# Revit family: Electronics_Desono_Biamp_Two-Way-Pendant-Mount-Loudspeaker_P60DT
name_source: partatom
category: Communication Devices
units: mm (PartAtom-declared; Revit-internal decimal feet)

## family parameters
Cut with Voids When Loaded = No
Host = Face
Maintain Annotation Orientation = No
OmniClass Number = 23.85.10.11.14.14.14
OmniClass Title = Loudspeakers
Part Type = Normal
Room Calculation Point = No
Round Connector Dimension = Use Diameter
Shared = No

## types (2) — shared parameters
Compliance = ETL listed to comply with UL Std 1480A,Certifed to CSA C22.2#62368-1Suspension system and Gripple cable fasteners listed per UL1598 and UL2239, TUV and CSA Class 3426-01 and Class 3426-81.
Connector Description = Euroblock; Low Impedance 8 ohms, 70/100V operation
Continuous Power Handling Nominal Impedance = 31V; 60W @ 16Ω (240W peak)
Controls = Power tap / low impedance selector switch
Default Elevation = 4' - 0"
Description = Desono™ P60DT Two-Way 6.5-Inch Pendant Mount Loudspeaker
Diameter = 0' - 11"
Height = 0' - 10 1/2"
Input Connection = 4-way Euroblock connector with permanent pass-through
Manufacturer = Biamp
Mounting Provisions = Two 5m (16.4 ft) wire suspension cables (one as primary support, one as a safety cable), of high tensile galvanized steel wire rope with integrated spring clips for attaching the cable to the bracket and Gripple cable fasteners.
Nominal Beamwidth  (H x V) = 120°, conical
Nominal Maximum SPL @ 1m = Peak-113dB; Continuous-107dB)
Nominal Sensitivity @ 1m = 1W-89dB; 2.83V 86dB)
Operating Environment = Indoor
Operating Mode = Passive
Operating Range (-10dB) = 75 Hz to 22 kHz
Product Documentation Link = https://downloads.biamp.com
Product Page URL = https://www.biamp.com
Product data url = https://www.bimobject.com
Protection = Self-resetting loudspeaker protection
Recommended Accessories = 75 Hz, 12dB/Oct High Pass
Recommended Amplifers = 60W - 120W @ 16Ω (31V - 44V)
Transducers = LF 1 x 6.5 (165 mm) coated paper cone HF 1 x 1 (25 mm) soft dome
Transformer = 70V: 60W, 30W, 15W, 7.5W, 3.75W;100V: 60W, 30W, 15W, 7.5W
URL = https://www.biamp.com
Weight = 8.60 lb

## per-type parameters (varying)
| type | Bracket Material | Grill Material | Housing Material |
| P60DT W | Biamp - Metal - White | Biamp - Plastic - White(Grid) | Biamp - Plastic - White |
| P60DT B | Biamp - Metal - Black | Biamp - Plastic - Black(Grid) | Biamp - Plastic - Black |

note: column(s) folded — value = type name in every type: Model

## geometry (parser evidence)
native form markers: Sweep x2
no freeform markers — native parametric forms only
